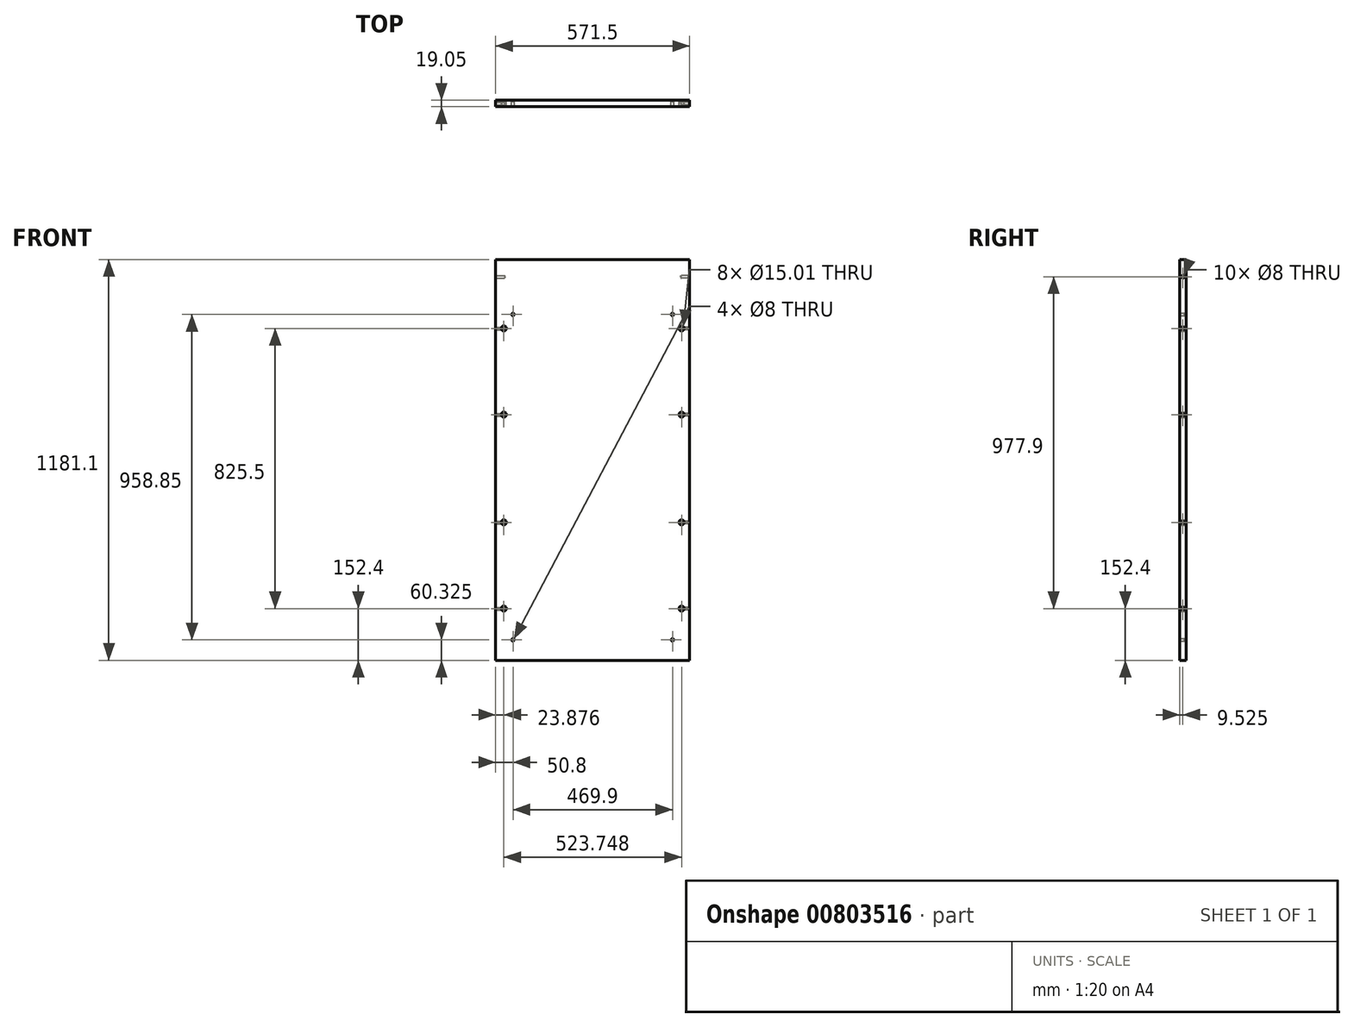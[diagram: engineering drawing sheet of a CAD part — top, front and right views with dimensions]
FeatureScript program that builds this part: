
annotation { "Feature Type Name" : "Feature", "Feature Type Description" : "" }
export const myFeature = defineFeature(function(context is Context, id is Id, definition is map)
    precondition{}
    {
        {
            var Q0;
            Q0=qCreatedBy(makeId("Front.planeOp"),FACE);
            var sketch = newSketch(context, id + "F0", { "sketchPlane" : qUnion([Q0])});
            skLineSegment(sketch, "E0.bottom", {"start": v(285.75, 590.55) * mm, "end": v(-285.75, 590.55) * mm});
            skLineSegment(sketch, "E0.top", {"start": v(285.75, -590.55) * mm, "end": v(-285.75, -590.55) * mm});
            skLineSegment(sketch, "E0.left", {"start": v(285.75, 590.55) * mm, "end": v(285.75, -590.55) * mm});
            skLineSegment(sketch, "E0.right", {"start": v(-285.75, 590.55) * mm, "end": v(-285.75, -590.55) * mm});
            skPoint(sketch, "E0.middle", {"position": v(0, 0) * mm});
            skSolve(sketch);
        }
        {
            var Q0;
            Q0=makeQuery(id+"F0.imprint","IMPRINT",FACE,{"disambiguationData":[TD([[makeQuery(id+"F0.imprint","IMPRINT",EDGE,{"derivedFrom":sQuery(id+"F0.wireOp",EDGE,"E0.bottom")}),1.0]])]});
            extrude(context, id + "F1", {"entities" : qUnion([Q0]), "depth" : 19.05 * mm, "offsetDistance" : 25.4 * mm});
        }
        {
            var Q0;
            Q0=makeQuery(id+"F1.opExtrude","CAP_FACE",FACE,{"disambiguationData":[OSD([sQuery(id+"F0.wireOp",EDGE,"E0.bottom"),sQuery(id+"F0.wireOp",EDGE,"E0.top"),sQuery(id+"F0.wireOp",EDGE,"E0.left"),sQuery(id+"F0.wireOp",EDGE,"E0.right")])],"isStart":false});
            var sketch = newSketch(context, id + "F2", { "sketchPlane" : qUnion([Q0])});
            skLineSegment(sketch, "E1", {"start": v(-285.75, 590.55) * mm, "end": v(-261.87, 590.55) * mm});
            skLineSegment(sketch, "E2", {"start": v(-261.87, 590.55) * mm, "end": v(-261.87, 387.35) * mm});
            skLineSegment(sketch, "E3", {"start": v(-261.87, 590.55) * mm, "end": v(-261.87, 133.35) * mm});
            skLineSegment(sketch, "E4", {"start": v(285.75, 590.55) * mm, "end": v(261.87, 590.55) * mm});
            skLineSegment(sketch, "E5", {"start": v(261.87, 590.55) * mm, "end": v(261.87, 387.35) * mm});
            skLineSegment(sketch, "E6", {"start": v(261.87, 590.55) * mm, "end": v(261.87, 133.35) * mm});
            skLineSegment(sketch, "E7", {"start": v(-285.75, -590.55) * mm, "end": v(-261.87, -590.55) * mm});
            skLineSegment(sketch, "E8", {"start": v(-261.87, -590.55) * mm, "end": v(-261.87, -438.15) * mm});
            skLineSegment(sketch, "E9", {"start": v(-261.87, -590.55) * mm, "end": v(-261.87, -184.15) * mm});
            skLineSegment(sketch, "E10", {"start": v(285.75, -590.55) * mm, "end": v(261.87, -590.55) * mm});
            skLineSegment(sketch, "E11", {"start": v(261.87, -590.55) * mm, "end": v(261.87, -438.15) * mm});
            skLineSegment(sketch, "E12", {"start": v(261.87, -590.55) * mm, "end": v(261.87, -184.15) * mm});
            skSolve(sketch);
        }
        {
            var Q0;
            Q0=sQuery(id+"F2.wireOp",VERTEX,"E2.end");
            var Q1;
            Q1=sQuery(id+"F2.wireOp",VERTEX,"E3.end");
            var Q2;
            Q2=sQuery(id+"F2.wireOp",VERTEX,"E9.end");
            var Q3;
            Q3=sQuery(id+"F2.wireOp",VERTEX,"E8.end");
            var Q4;
            Q4=sQuery(id+"F2.wireOp",VERTEX,"E11.end");
            var Q5;
            Q5=sQuery(id+"F2.wireOp",VERTEX,"E12.end");
            var Q6;
            Q6=sQuery(id+"F2.wireOp",VERTEX,"E6.end");
            var Q7;
            Q7=sQuery(id+"F2.wireOp",VERTEX,"E5.end");
            var Q8;
            Q8=makeQuery(id+"F1.opExtrude","SWEPT_BODY",BODY,{"disambiguationData":[OSD([sQuery(id+"F0.wireOp",EDGE,"E0.bottom"),sQuery(id+"F0.wireOp",EDGE,"E0.top"),sQuery(id+"F0.wireOp",EDGE,"E0.left"),sQuery(id+"F0.wireOp",EDGE,"E0.right")])]});
            hole(context, id + "F3", {"style" : HoleStyle.SIMPLE, "endStyle" : HoleEndStyle.BLIND, "holeDiameter" : 15 * mm, "majorDiameter" : 6.35 * mm, "holeDepth" : 14.22 * mm, "isTappedThrough" : true, "tappedDepth" : 12.7 * mm, "tapClearance" : 3, "startFromSketch" : true, "locations" : qUnion([Q0, Q1, Q2, Q3, Q4, Q5, Q6, Q7]), "scope" : qUnion([Q8])});
        }
        {
            var Q0;
            Q0=makeQuery(id+"F1.opExtrude","SWEPT_FACE",FACE,{"disambiguationData":[OSD([sQuery(id+"F0.wireOp",EDGE,"E0.left")])]});
            var sketch = newSketch(context, id + "F4", { "sketchPlane" : qUnion([Q0])});
            skLineSegment(sketch, "E13", {"start": v(-9.53, 590.55) * mm, "end": v(-9.53, 539.75) * mm});
            skLineSegment(sketch, "E14", {"start": v(-9.53, 590.55) * mm, "end": v(-9.53, 387.35) * mm});
            skLineSegment(sketch, "E15", {"start": v(-9.53, 590.55) * mm, "end": v(-9.53, 133.35) * mm});
            skLineSegment(sketch, "E16", {"start": v(-9.53, -590.55) * mm, "end": v(-9.53, -438.15) * mm});
            skLineSegment(sketch, "E17", {"start": v(-9.53, -590.55) * mm, "end": v(-9.53, -184.15) * mm});
            skPoint(sketch, "E18", {"position": v(-9.53, 539.75) * mm});
            skPoint(sketch, "E19", {"position": v(-9.53, 387.35) * mm});
            skPoint(sketch, "E20", {"position": v(-9.53, 133.35) * mm});
            skPoint(sketch, "E21", {"position": v(-9.53, -184.15) * mm});
            skPoint(sketch, "E22", {"position": v(-9.53, -438.15) * mm});
            skSolve(sketch);
        }
        {
            var Q0;
            Q0=sQuery(id+"F4.wireOp",VERTEX,"E18");
            var Q1;
            Q1=sQuery(id+"F4.wireOp",VERTEX,"E19");
            var Q2;
            Q2=sQuery(id+"F4.wireOp",VERTEX,"E20");
            var Q3;
            Q3=sQuery(id+"F4.wireOp",VERTEX,"E21");
            var Q4;
            Q4=sQuery(id+"F4.wireOp",VERTEX,"E22");
            var Q5;
            Q5=makeQuery(id+"F1.opExtrude","SWEPT_BODY",BODY,{"disambiguationData":[OSD([sQuery(id+"F0.wireOp",EDGE,"E0.bottom"),sQuery(id+"F0.wireOp",EDGE,"E0.top"),sQuery(id+"F0.wireOp",EDGE,"E0.left"),sQuery(id+"F0.wireOp",EDGE,"E0.right")])]});
            hole(context, id + "F5", {"style" : HoleStyle.SIMPLE, "endStyle" : HoleEndStyle.BLIND, "holeDiameter" : 8 * mm, "majorDiameter" : 6.35 * mm, "holeDepth" : 25.4 * mm, "isTappedThrough" : true, "tappedDepth" : 12.7 * mm, "tapClearance" : 3, "startFromSketch" : true, "locations" : qUnion([Q0, Q1, Q2, Q3, Q4]), "scope" : qUnion([Q5])});
        }
        {
            var Q0;
            Q0=makeQuery(id+"F1.opExtrude","SWEPT_FACE",FACE,{"disambiguationData":[OSD([sQuery(id+"F0.wireOp",EDGE,"E0.right")])]});
            var sketch = newSketch(context, id + "F6", { "sketchPlane" : qUnion([Q0])});
            skLineSegment(sketch, "E23", {"start": v(9.53, 590.55) * mm, "end": v(9.53, 539.75) * mm});
            skLineSegment(sketch, "E24", {"start": v(9.53, 590.55) * mm, "end": v(9.53, 387.35) * mm});
            skLineSegment(sketch, "E25", {"start": v(9.53, 590.55) * mm, "end": v(9.53, 133.35) * mm});
            skLineSegment(sketch, "E26", {"start": v(9.53, -590.55) * mm, "end": v(9.53, -438.15) * mm});
            skLineSegment(sketch, "E27", {"start": v(9.53, -590.55) * mm, "end": v(9.53, -184.15) * mm});
            skPoint(sketch, "E28", {"position": v(9.53, 539.75) * mm});
            skPoint(sketch, "E29", {"position": v(9.53, 387.35) * mm});
            skPoint(sketch, "E30", {"position": v(9.53, 133.35) * mm});
            skPoint(sketch, "E31", {"position": v(9.53, -184.15) * mm});
            skPoint(sketch, "E32", {"position": v(9.53, -438.15) * mm});
            skSolve(sketch);
        }
        {
            var Q0;
            Q0=sQuery(id+"F6.wireOp",VERTEX,"E28");
            var Q1;
            Q1=sQuery(id+"F6.wireOp",VERTEX,"E29");
            var Q2;
            Q2=sQuery(id+"F6.wireOp",VERTEX,"E25.end");
            var Q3;
            Q3=sQuery(id+"F6.wireOp",VERTEX,"E31");
            var Q4;
            Q4=sQuery(id+"F6.wireOp",VERTEX,"E32");
            var Q5;
            Q5=makeQuery(id+"F1.opExtrude","SWEPT_BODY",BODY,{"disambiguationData":[OSD([sQuery(id+"F0.wireOp",EDGE,"E0.bottom"),sQuery(id+"F0.wireOp",EDGE,"E0.top"),sQuery(id+"F0.wireOp",EDGE,"E0.left"),sQuery(id+"F0.wireOp",EDGE,"E0.right")])]});
            hole(context, id + "F7", {"style" : HoleStyle.SIMPLE, "endStyle" : HoleEndStyle.BLIND, "holeDiameter" : 8 * mm, "majorDiameter" : 6.35 * mm, "holeDepth" : 25.4 * mm, "isTappedThrough" : true, "tappedDepth" : 12.7 * mm, "tapClearance" : 3, "startFromSketch" : true, "locations" : qUnion([Q0, Q1, Q2, Q3, Q4]), "scope" : qUnion([Q5])});
        }
        {
            var Q0;
            Q0=makeQuery(id+"F1.opExtrude","CAP_FACE",FACE,{"disambiguationData":[OSD([sQuery(id+"F0.wireOp",EDGE,"E0.bottom"),sQuery(id+"F0.wireOp",EDGE,"E0.top"),sQuery(id+"F0.wireOp",EDGE,"E0.left"),sQuery(id+"F0.wireOp",EDGE,"E0.right")])],"isStart":false});
            var sketch = newSketch(context, id + "F8", { "sketchPlane" : qUnion([Q0])});
            skLineSegment(sketch, "E33", {"start": v(0, -590.55) * mm, "end": v(0, -530.23) * mm});
            skLineSegment(sketch, "E34", {"start": v(0, -530.23) * mm, "end": v(-234.95, -530.23) * mm});
            skLineSegment(sketch, "E35", {"start": v(0, -530.23) * mm, "end": v(234.95, -530.23) * mm});
            skPoint(sketch, "E36", {"position": v(-234.95, -530.23) * mm});
            skPoint(sketch, "E37", {"position": v(0, -530.23) * mm});
            skPoint(sketch, "E38", {"position": v(234.95, -530.23) * mm});
            skLineSegment(sketch, "E39", {"start": v(0, 590.55) * mm, "end": v(0, 428.62) * mm});
            skLineSegment(sketch, "E40", {"start": v(0, 428.62) * mm, "end": v(-234.95, 428.62) * mm});
            skLineSegment(sketch, "E41", {"start": v(0, 428.62) * mm, "end": v(234.95, 428.62) * mm});
            skPoint(sketch, "E42", {"position": v(-234.95, 428.62) * mm});
            skPoint(sketch, "E43", {"position": v(0, 428.62) * mm});
            skPoint(sketch, "E44", {"position": v(234.95, 428.62) * mm});
            skSolve(sketch);
        }
        {
            var Q0;
            Q0=sQuery(id+"F8.wireOp",VERTEX,"E36");
            var Q1;
            Q1=sQuery(id+"F8.wireOp",VERTEX,"E38");
            var Q2;
            Q2=sQuery(id+"F8.wireOp",VERTEX,"E42");
            var Q3;
            Q3=sQuery(id+"F8.wireOp",VERTEX,"E44");
            var Q4;
            Q4=makeQuery(id+"F1.opExtrude","SWEPT_BODY",BODY,{"disambiguationData":[OSD([sQuery(id+"F0.wireOp",EDGE,"E0.bottom"),sQuery(id+"F0.wireOp",EDGE,"E0.top"),sQuery(id+"F0.wireOp",EDGE,"E0.left"),sQuery(id+"F0.wireOp",EDGE,"E0.right")])]});
            hole(context, id + "F9", {"style" : HoleStyle.SIMPLE, "endStyle" : HoleEndStyle.BLIND, "holeDiameter" : 8 * mm, "majorDiameter" : 6.35 * mm, "holeDepth" : 14.22 * mm, "isTappedThrough" : true, "tappedDepth" : 12.7 * mm, "tapClearance" : 3, "startFromSketch" : true, "locations" : qUnion([Q0, Q1, Q2, Q3]), "scope" : qUnion([Q4])});
        }
    });
